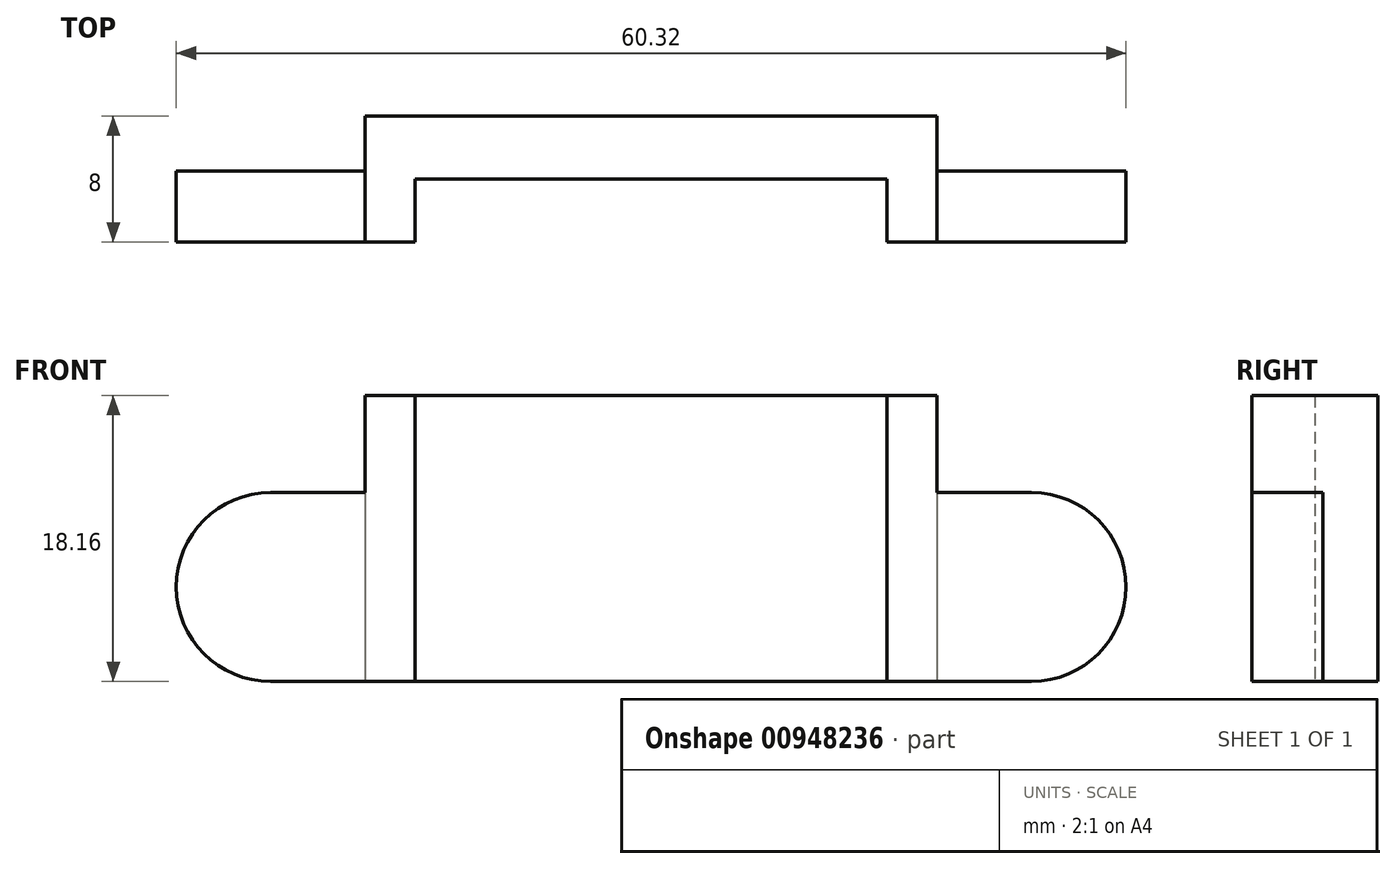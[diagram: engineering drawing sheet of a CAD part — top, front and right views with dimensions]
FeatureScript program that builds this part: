
annotation { "Feature Type Name" : "Feature", "Feature Type Description" : "" }
export const myFeature = defineFeature(function(context is Context, id is Id, definition is map)
    precondition{}
    {
        {
            var Q0;
            Q0=qCreatedBy(makeId("Top.planeOp"),FACE);
            var sketch = newSketch(context, id + "F0", { "sketchPlane" : qUnion([Q0])});
            skLineSegment(sketch, "E0", {"start": v(-18.16, 0) * mm, "end": v(-18.16, -8) * mm});
            skLineSegment(sketch, "E1", {"start": v(-18.16, -8) * mm, "end": v(-14.98, -8) * mm});
            skLineSegment(sketch, "E2", {"start": v(-14.98, -8) * mm, "end": v(-14.98, -4) * mm});
            skLineSegment(sketch, "E3", {"start": v(-14.98, -4) * mm, "end": v(14.98, -4) * mm});
            skLineSegment(sketch, "E4", {"start": v(14.98, -4) * mm, "end": v(14.98, -8) * mm});
            skLineSegment(sketch, "E5", {"start": v(14.98, -8) * mm, "end": v(18.16, -8) * mm});
            skLineSegment(sketch, "E6", {"start": v(18.16, -8) * mm, "end": v(18.16, 0) * mm});
            skLineSegment(sketch, "E7", {"start": v(18.16, 0) * mm, "end": v(-18.16, 0) * mm});
            skSolve(sketch);
        }
        {
            var Q0;
            Q0 = qSketchRegion(id + "F0", true);
            extrude(context, id + "F1", {"entities" : qUnion([Q0]), "depth" : 18.16 * mm, "offsetDistance" : 25 * mm});
        }
        {
            var Q0;
            Q0=makeQuery(id+"F1.opExtrude","CAP_FACE",FACE,{"disambiguationData":[OSD([sQuery(id+"F0.wireOp",EDGE,"E0"),sQuery(id+"F0.wireOp",EDGE,"E1"),sQuery(id+"F0.wireOp",EDGE,"E2"),sQuery(id+"F0.wireOp",EDGE,"E3"),sQuery(id+"F0.wireOp",EDGE,"E4"),sQuery(id+"F0.wireOp",EDGE,"E5"),sQuery(id+"F0.wireOp",EDGE,"E6"),sQuery(id+"F0.wireOp",EDGE,"E7")])],"isStart":true});
            var sketch = newSketch(context, id + "F2", { "sketchPlane" : qUnion([Q0])});
            skLineSegment(sketch, "E8.bottom", {"start": v(-18.16, 8) * mm, "end": v(-30.16, 8) * mm});
            skLineSegment(sketch, "E8.top", {"start": v(-18.16, 3.5) * mm, "end": v(-30.16, 3.5) * mm});
            skLineSegment(sketch, "E8.left", {"start": v(-18.16, 8) * mm, "end": v(-18.16, 3.5) * mm});
            skLineSegment(sketch, "E8.right", {"start": v(-30.16, 8) * mm, "end": v(-30.16, 3.5) * mm});
            skLineSegment(sketch, "E9.MirrorCS", {"start": v(30.16, 8) * mm, "end": v(30.16, 3.5) * mm});
            skLineSegment(sketch, "E10.MirrorCS", {"start": v(18.16, 3.5) * mm, "end": v(30.16, 3.5) * mm});
            skLineSegment(sketch, "E11.MirrorCS", {"start": v(18.16, 8) * mm, "end": v(30.16, 8) * mm});
            skLineSegment(sketch, "E12.MirrorCS", {"start": v(18.16, 8) * mm, "end": v(18.16, 3.5) * mm});
            skSolve(sketch);
        }
        {
            var Q0;
            Q0 = qSketchRegion(id + "F2", true);
            extrude(context, id + "F3", {"entities" : qUnion([Q0]), "operationType" : NewBodyOperationType.ADD, "oppositeDirection" : true, "depth" : 12 * mm, "offsetDistance" : 25 * mm});
        }
        {
            var Q0;
            Q0=makeQuery(id+"F3.opExtrude","CAP_EDGE",EDGE,{"disambiguationData":[OSD([sQuery(id+"F2.wireOp",EDGE,"E8.right")])],"isStart":false});
            var Q1;
            Q1=makeQuery(id+"F3.opExtrude","CAP_EDGE",EDGE,{"disambiguationData":[OSD([sQuery(id+"F2.wireOp",EDGE,"E8.right")])],"isStart":true});
            var Q2;
            Q2=makeQuery(id+"F3.opExtrude","CAP_EDGE",EDGE,{"disambiguationData":[OSD([sQuery(id+"F2.wireOp",EDGE,"E9.MirrorCS")])],"isStart":true});
            var Q3;
            Q3=makeQuery(id+"F3.opExtrude","CAP_EDGE",EDGE,{"disambiguationData":[OSD([sQuery(id+"F2.wireOp",EDGE,"E9.MirrorCS")])],"isStart":false});
            fillet(context, id + "F4", {"entities" : qUnion([Q0, Q1, Q2, Q3]), "radius" : 6 * mm, "tangentPropagation" : true, "allowEdgeOverflow" : false});
        }
    });
